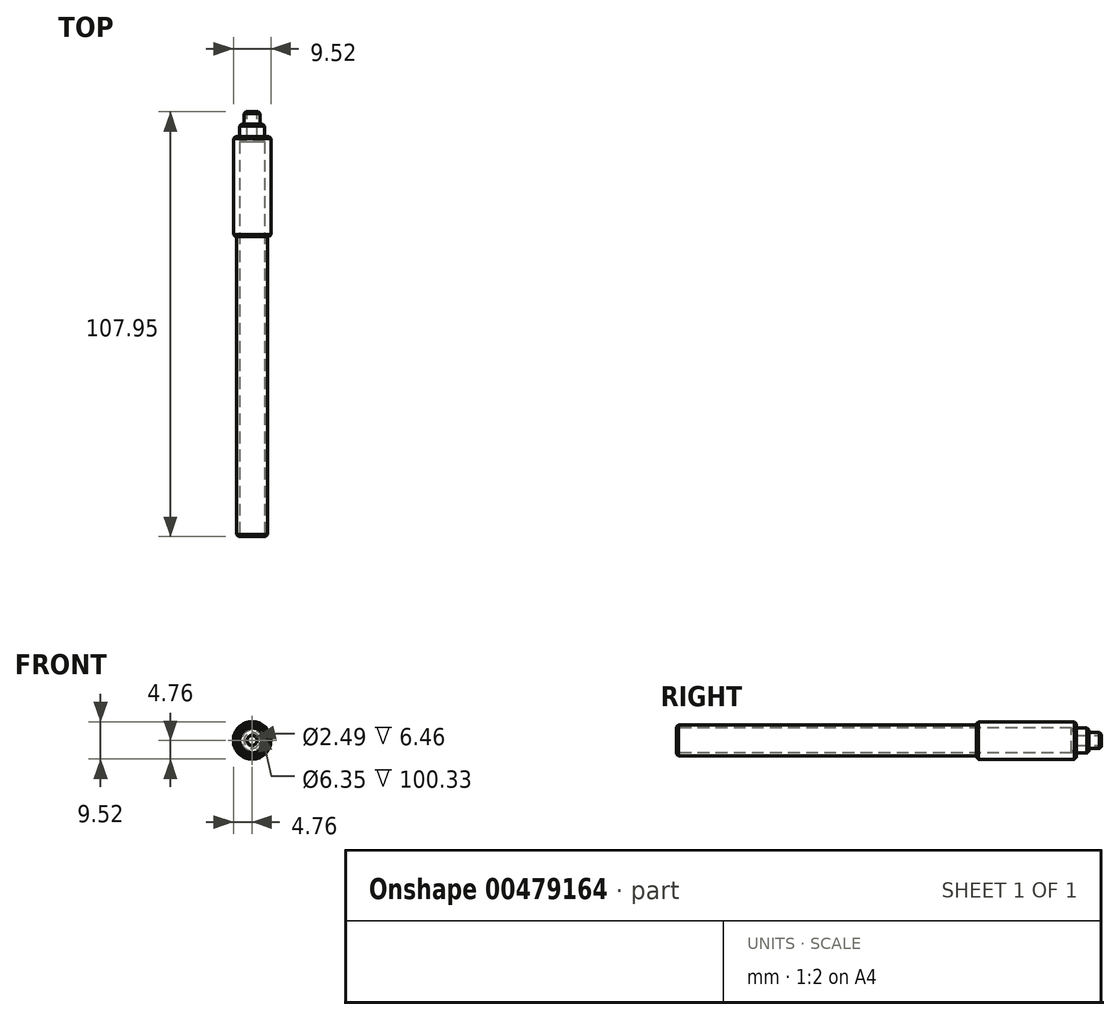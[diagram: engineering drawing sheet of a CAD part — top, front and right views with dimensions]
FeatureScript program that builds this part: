
annotation { "Feature Type Name" : "Feature", "Feature Type Description" : "" }
export const myFeature = defineFeature(function(context is Context, id is Id, definition is map)
    precondition{}
    {
        {
            var Q0;
            Q0=qCreatedBy(makeId("Front.planeOp"),FACE);
            var sketch = newSketch(context, id + "F0", { "sketchPlane" : qUnion([Q0])});
            skCircle(sketch, "E0", {"center": v(0, 0) * mm, "radius": 1.24 * mm});
            skCircle(sketch, "E1", {"center": v(0, 0) * mm, "radius": 2.03 * mm});
            skSolve(sketch);
        }
        {
            var Q0;
            Q0 = qSketchRegion(id + "F0", true);
            extrude(context, id + "F1", {"entities" : qUnion([Q0]), "depth" : 3.17 * mm});
        }
        {
            var Q0;
            Q0=makeQuery(id+"F1.opExtrude","CAP_FACE",FACE,{"disambiguationData":[OSD([sQuery(id+"F0.wireOp",EDGE,"E0"),sQuery(id+"F0.wireOp",EDGE,"E1")])],"isStart":false});
            var sketch = newSketch(context, id + "F2", { "sketchPlane" : qUnion([Q0])});
            skCircle(sketch, "E2", {"center": v(0, 0) * mm, "radius": 3.18 * mm});
            skSolve(sketch);
        }
        {
            var Q0;
            Q0 = qSketchRegion(id + "F2", true);
            extrude(context, id + "F3", {"entities" : qUnion([Q0]), "operationType" : NewBodyOperationType.ADD, "depth" : 3.17 * mm});
        }
        {
            var Q0;
            Q0=makeQuery(id+"F3.opExtrude","CAP_FACE",FACE,{"disambiguationData":[OSD([sQuery(id+"F2.wireOp",EDGE,"E2")])],"isStart":false});
            var sketch = newSketch(context, id + "F4", { "sketchPlane" : qUnion([Q0])});
            skCircle(sketch, "E3", {"center": v(0, 0) * mm, "radius": 4.76 * mm});
            skSolve(sketch);
        }
        {
            var Q0;
            Q0 = qSketchRegion(id + "F4", true);
            extrude(context, id + "F5", {"entities" : qUnion([Q0]), "operationType" : NewBodyOperationType.ADD, "depth" : 25.4 * mm});
        }
        {
            var Q0;
            Q0=makeQuery(id+"F5.opExtrude","CAP_FACE",FACE,{"disambiguationData":[OSD([sQuery(id+"F4.wireOp",EDGE,"E3")])],"isStart":false});
            var sketch = newSketch(context, id + "F6", { "sketchPlane" : qUnion([Q0])});
            skCircle(sketch, "E4", {"center": v(0, 0) * mm, "radius": 3.97 * mm});
            skSolve(sketch);
        }
        {
            var Q0;
            Q0 = qSketchRegion(id + "F6", true);
            extrude(context, id + "F7", {"entities" : qUnion([Q0]), "operationType" : NewBodyOperationType.ADD, "depth" : 76.2 * mm});
        }
        {
            var Q0;
            Q0=makeQuery(id+"F7.opExtrude","CAP_FACE",FACE,{"disambiguationData":[OSD([sQuery(id+"F6.wireOp",EDGE,"E4")])],"isStart":false});
            var sketch = newSketch(context, id + "F8", { "sketchPlane" : qUnion([Q0])});
            skPoint(sketch, "E5", {"position": v(0, 0) * mm});
            skSolve(sketch);
        }
        {
            var Q0;
            Q0=sQuery(id+"F8.wireOp",VERTEX,"E5");
            var Q1;
            Q1=makeQuery(id+"F1.opExtrude","SWEPT_BODY",BODY,{"disambiguationData":[OSD([sQuery(id+"F0.wireOp",EDGE,"E0"),sQuery(id+"F0.wireOp",EDGE,"E1")])]});
            hole(context, id + "F9", {"style" : HoleStyle.SIMPLE, "endStyle" : HoleEndStyle.BLIND, "holeDiameter" : 6.35 * mm, "holeDepth" : 100.33 * mm, "isTappedThrough" : true, "tappedDepth" : 12.7 * mm, "tapClearance" : 3, "locations" : qUnion([Q0]), "scope" : qUnion([Q1])});
        }
        {
            var Q0;
            Q0=sQuery(id+"F8.wireOp",VERTEX,"E5");
            var Q1;
            Q1=makeQuery(id+"F1.opExtrude","SWEPT_BODY",BODY,{"disambiguationData":[OSD([sQuery(id+"F0.wireOp",EDGE,"E0"),sQuery(id+"F0.wireOp",EDGE,"E1")])]});
            hole(context, id + "F10", {"style" : HoleStyle.SIMPLE, "endStyle" : HoleEndStyle.THROUGH, "holeDiameter" : 2.5 * mm, "isTappedThrough" : true, "tappedDepth" : 12.7 * mm, "tapClearance" : 3, "locations" : qUnion([Q0]), "scope" : qUnion([Q1])});
        }
        {
            var Q0;
            Q0=makeQuery(id+"F1.opExtrude","CAP_EDGE",EDGE,{"disambiguationData":[OSD([sQuery(id+"F0.wireOp",EDGE,"E1")])],"isStart":true});
            var Q1;
            Q1=makeQuery(id+"F3.opExtrude","CAP_EDGE",EDGE,{"disambiguationData":[OSD([sQuery(id+"F2.wireOp",EDGE,"E2")])],"isStart":true});
            var Q2;
            Q2=makeQuery(id+"F5.opExtrude","CAP_EDGE",EDGE,{"disambiguationData":[OSD([sQuery(id+"F4.wireOp",EDGE,"E3")])],"isStart":true});
            var Q3;
            Q3=makeQuery(id+"F5.opExtrude","CAP_EDGE",EDGE,{"disambiguationData":[OSD([sQuery(id+"F4.wireOp",EDGE,"E3")])],"isStart":false});
            var Q4;
            Q4=makeQuery(id+"F7.opExtrude","CAP_EDGE",EDGE,{"disambiguationData":[OSD([sQuery(id+"F6.wireOp",EDGE,"E4")])],"isStart":false});
            chamfer(context, id + "F11", {"entities" : qUnion([Q0, Q1, Q2, Q3, Q4]), "width" : 0.5 * mm, "tangentPropagation" : true});
        }
    });
